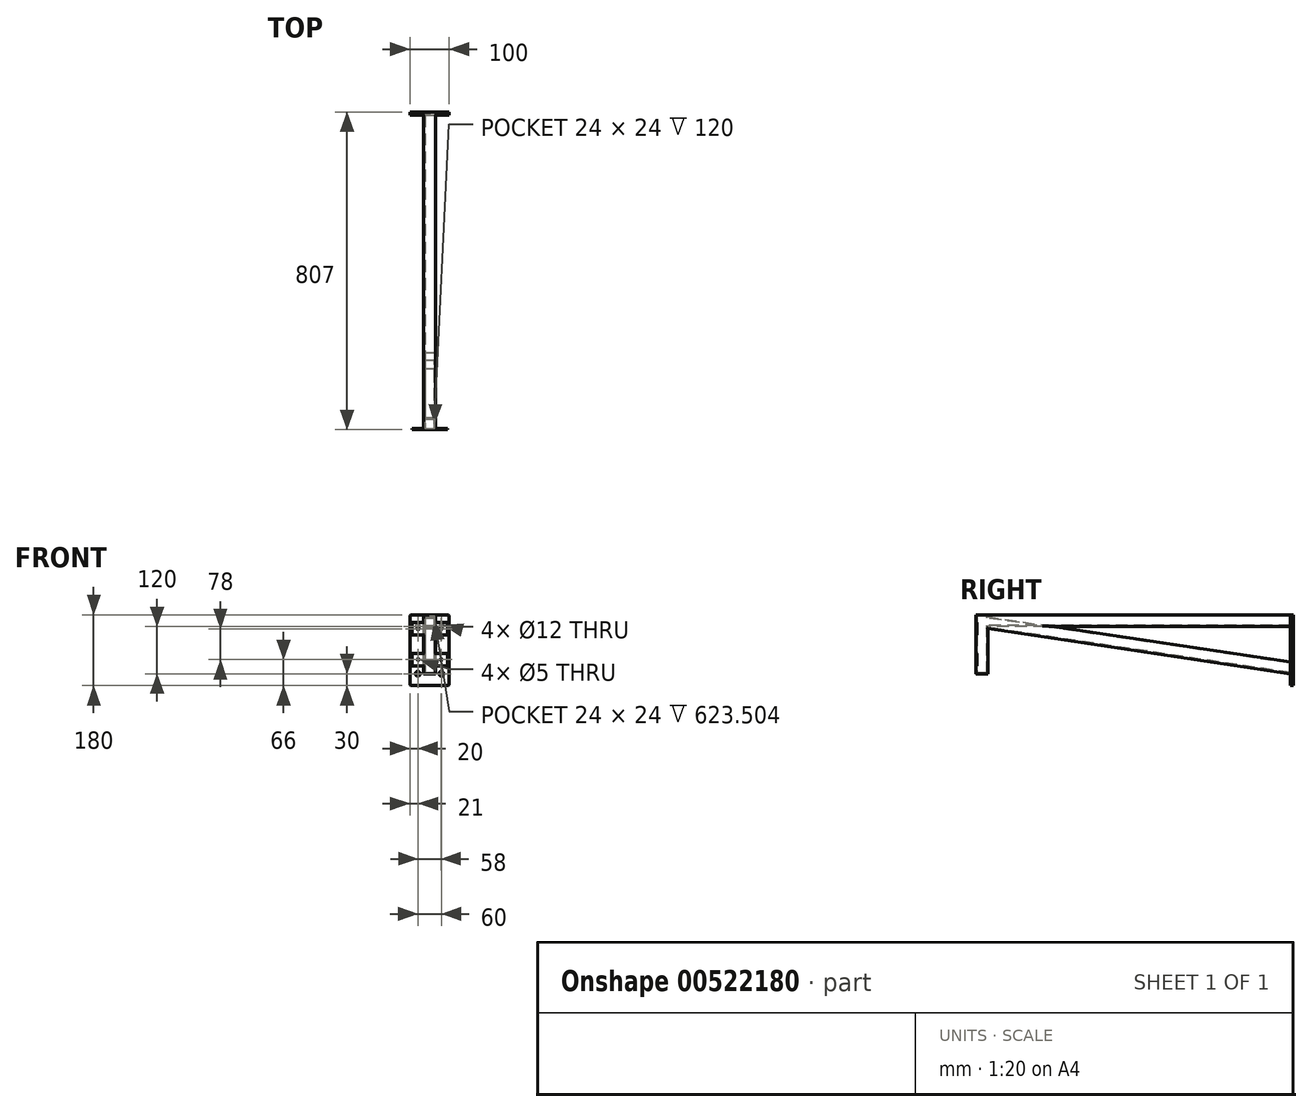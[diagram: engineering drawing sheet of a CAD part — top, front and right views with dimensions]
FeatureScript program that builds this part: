
annotation { "Feature Type Name" : "Feature", "Feature Type Description" : "" }
export const myFeature = defineFeature(function(context is Context, id is Id, definition is map)
    precondition{}
    {
        {
            var Q0;
            Q0=qCreatedBy(makeId("Front.planeOp"),FACE);
            var sketch = newSketch(context, id + "F0", { "sketchPlane" : qUnion([Q0])});
            skLineSegment(sketch, "E0.bottom", {"start": v(50, 90) * mm, "end": v(-50, 90) * mm});
            skLineSegment(sketch, "E0.top", {"start": v(50, -90) * mm, "end": v(-50, -90) * mm});
            skLineSegment(sketch, "E0.left", {"start": v(50, 90) * mm, "end": v(50, -90) * mm});
            skLineSegment(sketch, "E0.right", {"start": v(-50, 90) * mm, "end": v(-50, -90) * mm});
            skPoint(sketch, "E0.middle", {"position": v(0, 0) * mm});
            skCircle(sketch, "E1", {"center": v(-30, 60) * mm, "radius": 6 * mm});
            skCircle(sketch, "E2", {"center": v(30, 60) * mm, "radius": 6 * mm});
            skCircle(sketch, "E3", {"center": v(30, -60) * mm, "radius": 6 * mm});
            skCircle(sketch, "E4", {"center": v(-30, -60) * mm, "radius": 6 * mm});
            skSolve(sketch);
        }
        {
            var Q0;
            Q0=qSketchRegion(id+"F0",true);
            extrude(context, id + "F1", {"entities" : qUnion([Q0]), "depth" : 8 * mm, "offsetDistance" : 25 * mm});
        }
        {
            var Q0;
            Q0=makeQuery(id+"F1.opExtrude","SWEPT_EDGE",EDGE,{"disambiguationData":[OSD([sQuery(id+"F0.wireOp",EDGE,"E0.bottom"),sQuery(id+"F0.wireOp",EDGE,"E0.left")])]});
            var Q1;
            Q1=makeQuery(id+"F1.opExtrude","SWEPT_EDGE",EDGE,{"disambiguationData":[OSD([sQuery(id+"F0.wireOp",EDGE,"E0.top"),sQuery(id+"F0.wireOp",EDGE,"E0.left")])]});
            var Q2;
            Q2=makeQuery(id+"F1.opExtrude","SWEPT_EDGE",EDGE,{"disambiguationData":[OSD([sQuery(id+"F0.wireOp",EDGE,"E0.top"),sQuery(id+"F0.wireOp",EDGE,"E0.right")])]});
            var Q3;
            Q3=makeQuery(id+"F1.opExtrude","SWEPT_EDGE",EDGE,{"disambiguationData":[OSD([sQuery(id+"F0.wireOp",EDGE,"E0.bottom"),sQuery(id+"F0.wireOp",EDGE,"E0.right")])]});
            chamfer(context, id + "F2", {"entities" : qUnion([Q0, Q1, Q2, Q3]), "width" : 2 * mm, "tangentPropagation" : true});
        }
        {
            var Q0;
            Q0=qCreatedBy(makeId("Right.planeOp"),FACE);
            var sketch = newSketch(context, id + "F3", { "sketchPlane" : qUnion([Q0])});
            skLineSegment(sketch, "E5", {"start": v(-8, 90) * mm, "end": v(-807, 90) * mm});
            skLineSegment(sketch, "E6", {"start": v(-807, 90) * mm, "end": v(-807, -57) * mm});
            skLineSegment(sketch, "E7", {"start": v(-779, 55) * mm, "end": v(-8, -60) * mm});
            skSolve(sketch);
        }
        {
            var Q0;
            Q0=makeQuery(id+"F1.opExtrude","CAP_FACE",FACE,{"disambiguationData":[OSD([sQuery(id+"F0.wireOp",EDGE,"E0.bottom"),sQuery(id+"F0.wireOp",EDGE,"E0.top"),sQuery(id+"F0.wireOp",EDGE,"E0.left"),sQuery(id+"F0.wireOp",EDGE,"E0.right"),sQuery(id+"F0.wireOp",EDGE,"E1"),sQuery(id+"F0.wireOp",EDGE,"E2"),sQuery(id+"F0.wireOp",EDGE,"E3"),sQuery(id+"F0.wireOp",EDGE,"E4")])],"isStart":false});
            var sketch = newSketch(context, id + "F4", { "sketchPlane" : qUnion([Q0])});
            skLineSegment(sketch, "E8.bottom", {"start": v(-13, 90) * mm, "end": v(13, 90) * mm});
            skLineSegment(sketch, "E8.top", {"start": v(-13, 60) * mm, "end": v(13, 60) * mm});
            skLineSegment(sketch, "E8.left", {"start": v(-15, 88) * mm, "end": v(-15, 62) * mm});
            skLineSegment(sketch, "E8.right", {"start": v(15, 88) * mm, "end": v(15, 62) * mm});
            skLineSegment(sketch, "E9.0", {"start": v(-12, 87) * mm, "end": v(12, 87) * mm});
            skLineSegment(sketch, "E9.1", {"start": v(-12, 87) * mm, "end": v(-12, 63) * mm});
            skLineSegment(sketch, "E9.2", {"start": v(-12, 63) * mm, "end": v(12, 63) * mm});
            skLineSegment(sketch, "E9.3", {"start": v(12, 87) * mm, "end": v(12, 63) * mm});
            skPoint(sketch, "E10.visualSharp", {"position": v(-15, 90) * mm});
            skArc(sketch, "E10.filletArc", {"start": v(-13, 90) * mm, "mid": v(-14.41, 89.41) * mm, "end": v(-15, 88) * mm});
            skPoint(sketch, "E11.visualSharp", {"position": v(15, 90) * mm});
            skArc(sketch, "E11.filletArc", {"start": v(15, 88) * mm, "mid": v(14.41, 89.41) * mm, "end": v(13, 90) * mm});
            skPoint(sketch, "E12.visualSharp", {"position": v(15, 60) * mm});
            skArc(sketch, "E12.filletArc", {"start": v(13, 60) * mm, "mid": v(14.41, 60.59) * mm, "end": v(15, 62) * mm});
            skPoint(sketch, "E13.visualSharp", {"position": v(-15, 60) * mm});
            skArc(sketch, "E13.filletArc", {"start": v(-15, 62) * mm, "mid": v(-14.41, 60.59) * mm, "end": v(-13, 60) * mm});
            skLineSegment(sketch, "E14.0.1.0", {"start": v(-13, -30) * mm, "end": v(13, -30) * mm});
            skLineSegment(sketch, "E14.0.1.1", {"start": v(-15, -32) * mm, "end": v(-15, -58) * mm});
            skPoint(sketch, "E14.0.1.2", {"position": v(15, -30) * mm});
            skLineSegment(sketch, "E14.0.1.3", {"start": v(-12, -33) * mm, "end": v(12, -33) * mm});
            skLineSegment(sketch, "E14.0.1.4", {"start": v(-12, -33) * mm, "end": v(-12, -57) * mm});
            skLineSegment(sketch, "E14.0.1.5", {"start": v(-13, -60) * mm, "end": v(13, -60) * mm});
            skLineSegment(sketch, "E14.0.1.6", {"start": v(-12, -57) * mm, "end": v(12, -57) * mm});
            skPoint(sketch, "E14.0.1.7", {"position": v(-15, -30) * mm});
            skPoint(sketch, "E14.0.1.8", {"position": v(15, -60) * mm});
            skLineSegment(sketch, "E14.0.1.9", {"start": v(15, -32) * mm, "end": v(15, -58) * mm});
            skPoint(sketch, "E14.0.1.10", {"position": v(-15, -60) * mm});
            skLineSegment(sketch, "E14.0.1.11", {"start": v(12, -33) * mm, "end": v(12, -57) * mm});
            skArc(sketch, "E14.0.1.12", {"start": v(-15, -58) * mm, "mid": v(-14.41, -59.41) * mm, "end": v(-13, -60) * mm});
            skArc(sketch, "E14.0.1.13", {"start": v(13, -60) * mm, "mid": v(14.41, -59.41) * mm, "end": v(15, -58) * mm});
            skArc(sketch, "E14.0.1.14", {"start": v(15, -32) * mm, "mid": v(14.41, -30.59) * mm, "end": v(13, -30) * mm});
            skArc(sketch, "E14.0.1.15", {"start": v(-13, -30) * mm, "mid": v(-14.41, -30.59) * mm, "end": v(-15, -32) * mm});
            skLineSegment(sketch, "E14.direction1", {"start": v(-15, 60) * mm, "end": v(10, 60) * mm, "construction": true});
            skLineSegment(sketch, "E14.direction2", {"start": v(-15, 60) * mm, "end": v(-15, -60) * mm, "construction": true});
            skSolve(sketch);
        }
        {
            var Q0;
            Q0=makeQuery(id+"F4.imprint","IMPRINT",FACE,{"disambiguationData":[TD([[makeQuery(id+"F4.imprint","IMPRINT",EDGE,{"derivedFrom":sQuery(id+"F4.wireOp",EDGE,"E8.bottom")}),1.0]])]});
            var Q1;
            Q1=sQuery(id+"F3.wireOp",EDGE,"E5");
            var Q2;
            Q2=sQuery(id+"F3.wireOp",EDGE,"E6");
            sweep(context, id + "F5", {"profiles" : qUnion([Q0]), "path" : qUnion([Q1, Q2])});
        }
        {
            var Q0;
            Q0=makeQuery(id+"F4.imprint","IMPRINT",FACE,{"disambiguationData":[TD([[makeQuery(id+"F4.imprint","IMPRINT",EDGE,{"derivedFrom":sQuery(id+"F4.wireOp",EDGE,"E14.0.1.0")}),-1.0]])]});
            var Q1;
            Q1=sQuery(id+"F3.wireOp",EDGE,"E7");
            sweep(context, id + "F6", {"operationType" : NewBodyOperationType.ADD, "profiles" : qUnion([Q0]), "path" : qUnion([Q1]), "keepProfileOrientation" : true});
        }
        {
            var Q0;
            Q0=makeQuery(id+"F5.opSweep","CAP_FACE",FACE,{"disambiguationData":[OSD([sQuery(id+"F3.wireOp",VERTEX,"E6.end"),sQuery(id+"F4.wireOp",EDGE,"E8.bottom"),sQuery(id+"F4.wireOp",EDGE,"E8.top"),sQuery(id+"F4.wireOp",EDGE,"E8.left"),sQuery(id+"F4.wireOp",EDGE,"E8.right"),sQuery(id+"F4.wireOp",EDGE,"E9.0"),sQuery(id+"F4.wireOp",EDGE,"E9.1"),sQuery(id+"F4.wireOp",EDGE,"E9.2"),sQuery(id+"F4.wireOp",EDGE,"E9.3"),sQuery(id+"F4.wireOp",EDGE,"E10.filletArc"),sQuery(id+"F4.wireOp",EDGE,"E11.filletArc"),sQuery(id+"F4.wireOp",EDGE,"E12.filletArc"),sQuery(id+"F4.wireOp",EDGE,"E13.filletArc")])],"isStart":false});
            var sketch = newSketch(context, id + "F7", { "sketchPlane" : qUnion([Q0])});
            skLineSegment(sketch, "E15.0", {"start": v(-15, 805) * mm, "end": v(-15, 779) * mm});
            skPoint(sketch, "E16.0", {"position": v(-14.41, 777.59) * mm});
            skArc(sketch, "E17.0", {"start": v(-15, 779) * mm, "mid": v(-14.41, 777.59) * mm, "end": v(-13, 777) * mm});
            skLineSegment(sketch, "E18.0", {"start": v(-13, 777) * mm, "end": v(13, 777) * mm});
            skArc(sketch, "E19.0", {"start": v(13, 777) * mm, "mid": v(14.41, 777.59) * mm, "end": v(15, 779) * mm});
            skLineSegment(sketch, "E20.0", {"start": v(15, 805) * mm, "end": v(15, 779) * mm});
            skArc(sketch, "E21.0", {"start": v(15, 805) * mm, "mid": v(14.41, 806.41) * mm, "end": v(13, 807) * mm});
            skLineSegment(sketch, "E22.0", {"start": v(13, 807) * mm, "end": v(-13, 807) * mm});
            skArc(sketch, "E23.0", {"start": v(-13, 807) * mm, "mid": v(-14.41, 806.41) * mm, "end": v(-15, 805) * mm});
            skSolve(sketch);
        }
        {
            var Q0;
            Q0=qSketchRegion(id+"F7",true);
            extrude(context, id + "F8", {"entities" : qUnion([Q0]), "operationType" : NewBodyOperationType.ADD, "depth" : 3 * mm, "offsetDistance" : 25 * mm});
        }
        {
            var Q0;
            Q0=makeQuery(id+"F8.boolean.opBoolean","MERGE",FACE,{"derivedFrom":[makeQuery(id+"F5.opSweep","SWEPT_FACE",FACE,{"disambiguationData":[OSD([sQuery(id+"F3.wireOp",EDGE,"E6"),sQuery(id+"F4.wireOp",EDGE,"E8.bottom")])]}),makeQuery(id+"F8.opExtrude","SWEPT_FACE",FACE,{"disambiguationData":[OSD([sQuery(id+"F7.wireOp",EDGE,"E22.0")])]})]});
            var sketch = newSketch(context, id + "F9", { "sketchPlane" : qUnion([Q0])});
            skLineSegment(sketch, "E24.bottom", {"start": v(13, 70) * mm, "end": v(45, 70) * mm});
            skLineSegment(sketch, "E24.top", {"start": v(13, 38) * mm, "end": v(45, 38) * mm});
            skLineSegment(sketch, "E24.left", {"start": v(13, 70) * mm, "end": v(13, 38) * mm});
            skLineSegment(sketch, "E24.right", {"start": v(45, 70) * mm, "end": v(45, 38) * mm});
            skLineSegment(sketch, "E25.bottom", {"start": v(13, -8) * mm, "end": v(45, -8) * mm});
            skLineSegment(sketch, "E25.top", {"start": v(13, -40) * mm, "end": v(45, -40) * mm});
            skLineSegment(sketch, "E25.left", {"start": v(13, -8) * mm, "end": v(13, -40) * mm});
            skLineSegment(sketch, "E25.right", {"start": v(45, -8) * mm, "end": v(45, -40) * mm});
            skCircle(sketch, "E26", {"center": v(29, 54) * mm, "radius": 2.5 * mm});
            skPoint(sketch, "E26.centerSnap0", {"position": v(29, 38) * mm});
            skPoint(sketch, "E26.centerSnap1", {"position": v(45, 54) * mm});
            skCircle(sketch, "E27", {"center": v(29, -24) * mm, "radius": 2.5 * mm});
            skPoint(sketch, "E27.centerSnap0", {"position": v(45, -24) * mm});
            skPoint(sketch, "E27.centerSnap1", {"position": v(29, -40) * mm});
            skCircle(sketch, "E28.MirrorC", {"center": v(-29, 54) * mm, "radius": 2.5 * mm});
            skLineSegment(sketch, "E29.MirrorCS", {"start": v(-45, 70) * mm, "end": v(-45, 38) * mm});
            skLineSegment(sketch, "E30.MirrorCS", {"start": v(-13, 38) * mm, "end": v(-45, 38) * mm});
            skLineSegment(sketch, "E31.MirrorCS", {"start": v(-13, -8) * mm, "end": v(-13, -40) * mm});
            skLineSegment(sketch, "E32.MirrorCS", {"start": v(-45, -8) * mm, "end": v(-45, -40) * mm});
            skPoint(sketch, "E33.MirrorP", {"position": v(-45, 54) * mm});
            skPoint(sketch, "E34.MirrorP", {"position": v(-29, -40) * mm});
            skPoint(sketch, "E35.MirrorP", {"position": v(-29, 38) * mm});
            skLineSegment(sketch, "E36.MirrorCS", {"start": v(-13, 70) * mm, "end": v(-45, 70) * mm});
            skPoint(sketch, "E37.MirrorP", {"position": v(-45, -24) * mm});
            skCircle(sketch, "E38.MirrorC", {"center": v(-29, -24) * mm, "radius": 2.5 * mm});
            skLineSegment(sketch, "E39.MirrorCS", {"start": v(-13, -40) * mm, "end": v(-45, -40) * mm});
            skLineSegment(sketch, "E40.MirrorCS", {"start": v(-13, 70) * mm, "end": v(-13, 38) * mm});
            skLineSegment(sketch, "E41.MirrorCS", {"start": v(-13, -8) * mm, "end": v(-45, -8) * mm});
            skSolve(sketch);
        }
        {
            var Q0;
            Q0 = qSketchRegion(id + "F9", true);
            extrude(context, id + "F10", {"entities" : qUnion([Q0]), "operationType" : NewBodyOperationType.ADD, "oppositeDirection" : true, "depth" : 3 * mm, "offsetDistance" : 25 * mm});
        }
    });
